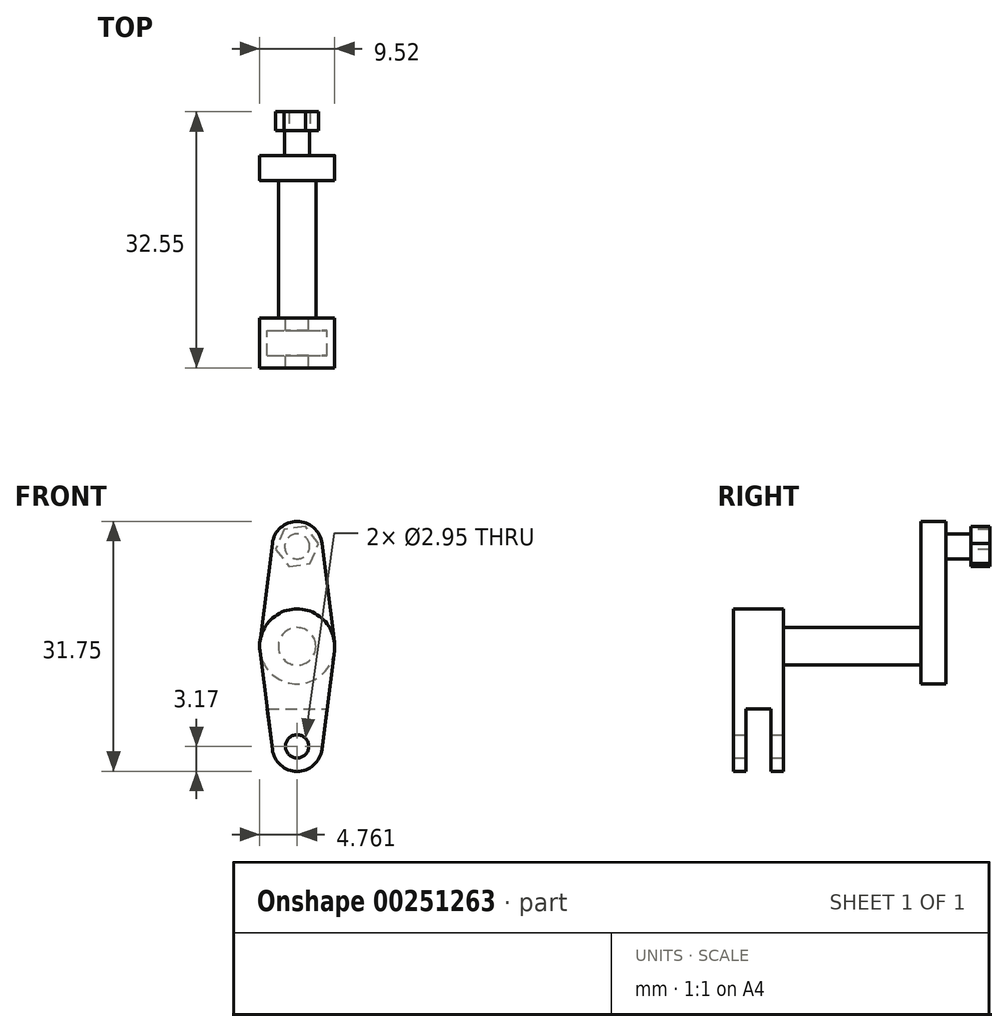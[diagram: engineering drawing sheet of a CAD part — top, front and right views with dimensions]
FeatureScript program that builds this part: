
annotation { "Feature Type Name" : "Feature", "Feature Type Description" : "" }
export const myFeature = defineFeature(function(context is Context, id is Id, definition is map)
    precondition{}
    {
        {
            var Q0;
            Q0=qCreatedBy(makeId("Front.planeOp"),FACE);
            var sketch = newSketch(context, id + "F0", { "sketchPlane" : qUnion([Q0])});
            skLineSegment(sketch, "E0.bottom", {"start": v(30.87, 50.07) * mm, "end": v(40.4, 50.07) * mm});
            skLineSegment(sketch, "E0.top", {"start": v(30.87, 15.15) * mm, "end": v(40.4, 15.15) * mm});
            skLineSegment(sketch, "E0.left", {"start": v(30.87, 50.07) * mm, "end": v(30.87, 15.15) * mm});
            skLineSegment(sketch, "E0.right", {"start": v(40.4, 50.07) * mm, "end": v(40.4, 15.15) * mm});
            skCircle(sketch, "E1", {"center": v(35.63, 45.31) * mm, "radius": 1.47 * mm});
            skCircle(sketch, "E2", {"center": v(35.63, 19.91) * mm, "radius": 1.47 * mm});
            skCircle(sketch, "E3", {"center": v(35.63, 32.61) * mm, "radius": 4.76 * mm});
            skCircle(sketch, "E4", {"center": v(35.63, 45.31) * mm, "radius": 3.18 * mm});
            skCircle(sketch, "E5", {"center": v(35.63, 19.91) * mm, "radius": 3.18 * mm});
            skLineSegment(sketch, "E6", {"start": v(32.48, 45.7) * mm, "end": v(30.9, 33.2) * mm});
            skLineSegment(sketch, "E7", {"start": v(38.78, 45.7) * mm, "end": v(40.36, 33.2) * mm});
            skLineSegment(sketch, "E8", {"start": v(30.9, 32.01) * mm, "end": v(32.48, 19.51) * mm});
            skLineSegment(sketch, "E9", {"start": v(40.36, 32.01) * mm, "end": v(38.78, 19.51) * mm});
            skSolve(sketch);
        }
        {
            var Q0;
            Q0=makeQuery(id+"F0.imprint","IMPRINT",FACE,{"disambiguationData":[TD([[makeQuery(id+"F0.imprint","IMPRINT",EDGE,{"derivedFrom":sQuery(id+"F0.wireOp",EDGE,"E1")}),1.0]])]});
            var Q1;
            Q1=makeQuery(id+"F0.imprint","IMPRINT",FACE,{"disambiguationData":[TD([[makeQuery(id+"F0.imprint","IMPRINT",EDGE,{"derivedFrom":sQuery(id+"F0.wireOp",EDGE,"E1")}),-1.0]])]});
            var Q2;
            {var subQ0=sQuery(id+"F0.wireOp",EDGE,"E6");Q2=makeQuery(id+"F0.imprint","IMPRINT",FACE,{"disambiguationData":[TD([[makeQuery(id+"F0.imprint","IMPRINT",EDGE,{"derivedFrom":subQ0}),1.0]])]});}
            var Q3;
            {var subQ0=sQuery(id+"F0.wireOp",EDGE,"E3");var subQ4=makeQuery(id+"F0.imprint","INTERSECT",VERTEX,{"derivedFrom":[subQ0,sQuery(id+"F0.wireOp",EDGE,"E7")]});Q3=makeQuery(id+"F0.imprint","IMPRINT",FACE,{"disambiguationData":[TD([[makeQuery(id+"F0.imprint","IMPRINT",EDGE,{"disambiguationData":[TD([[subQ4,1.0]])],"derivedFrom":subQ0}),1.0]])]});}
            extrude(context, id + "F1", {"entities" : qUnion([Q0, Q1, Q2, Q3]), "depth" : 3.17 * mm});
        }
        {
            var Q0;
            Q0=makeQuery(id+"F1.opExtrude","CAP_FACE",FACE,{"disambiguationData":[OSD([sQuery(id+"F0.wireOp",EDGE,"E3"),sQuery(id+"F0.wireOp",EDGE,"E4"),sQuery(id+"F0.wireOp",EDGE,"E6"),sQuery(id+"F0.wireOp",EDGE,"E7")])],"isStart":true});
            var sketch = newSketch(context, id + "F2", { "sketchPlane" : qUnion([Q0])});
            skCircle(sketch, "E10", {"center": v(-35.63, 45.31) * mm, "radius": 1.59 * mm});
            skSolve(sketch);
        }
        {
            var Q0;
            Q0 = qSketchRegion(id + "F2", true);
            extrude(context, id + "F3", {"entities" : qUnion([Q0]), "operationType" : NewBodyOperationType.ADD, "depth" : 3.17 * mm});
        }
        {
            var Q0;
            Q0=makeQuery(id+"F3.opExtrude","CAP_FACE",FACE,{"disambiguationData":[OSD([sQuery(id+"F2.wireOp",EDGE,"E10")])],"isStart":false});
            var sketch = newSketch(context, id + "F4", { "sketchPlane" : qUnion([Q0])});
            skCircle(sketch, "E11.cCircle", {"center": v(-35.63, 45.31) * mm, "radius": 2.38 * mm, "construction": true});
            skLineSegment(sketch, "E11.0", {"start": v(-32.9, 44.95) * mm, "end": v(-34.58, 42.77) * mm});
            skLineSegment(sketch, "E11.1", {"start": v(-34.58, 42.77) * mm, "end": v(-37.3, 43.13) * mm});
            skLineSegment(sketch, "E11.2", {"start": v(-37.3, 43.13) * mm, "end": v(-38.36, 45.67) * mm});
            skLineSegment(sketch, "E11.3", {"start": v(-38.36, 45.67) * mm, "end": v(-36.69, 47.85) * mm});
            skLineSegment(sketch, "E11.4", {"start": v(-36.69, 47.85) * mm, "end": v(-33.96, 47.5) * mm});
            skLineSegment(sketch, "E11.5", {"start": v(-33.96, 47.5) * mm, "end": v(-32.9, 44.95) * mm});
            skPoint(sketch, "E11.0.midPoint", {"position": v(-33.74, 43.86) * mm});
            skSolve(sketch);
        }
        {
            var Q0;
            Q0 = qSketchRegion(id + "F4", true);
            extrude(context, id + "F5", {"entities" : qUnion([Q0]), "operationType" : NewBodyOperationType.ADD, "depth" : 2.38 * mm});
        }
        {
            var Q0;
            Q0=makeQuery(id+"F1.opExtrude","CAP_FACE",FACE,{"disambiguationData":[OSD([sQuery(id+"F0.wireOp",EDGE,"E3"),sQuery(id+"F0.wireOp",EDGE,"E4"),sQuery(id+"F0.wireOp",EDGE,"E6"),sQuery(id+"F0.wireOp",EDGE,"E7")])],"isStart":false});
            var sketch = newSketch(context, id + "F6", { "sketchPlane" : qUnion([Q0])});
            skCircle(sketch, "E12", {"center": v(35.63, 32.61) * mm, "radius": 2.38 * mm});
            skSolve(sketch);
        }
        {
            var Q0;
            Q0 = qSketchRegion(id + "F6", true);
            extrude(context, id + "F7", {"entities" : qUnion([Q0]), "operationType" : NewBodyOperationType.ADD, "depth" : 17.46 * mm});
        }
        {
            var Q0;
            Q0=makeQuery(id+"F7.opExtrude","CAP_FACE",FACE,{"disambiguationData":[OSD([sQuery(id+"F6.wireOp",EDGE,"E12")])],"isStart":false});
            var sketch = newSketch(context, id + "F8", { "sketchPlane" : qUnion([Q0])});
            skCircle(sketch, "E13", {"center": v(35.63, 32.61) * mm, "radius": 4.76 * mm});
            skCircle(sketch, "E14", {"center": v(35.63, 19.91) * mm, "radius": 3.18 * mm});
            skLineSegment(sketch, "E15", {"start": v(30.9, 32.01) * mm, "end": v(32.48, 19.51) * mm});
            skLineSegment(sketch, "E16", {"start": v(40.36, 32.01) * mm, "end": v(38.78, 19.51) * mm});
            skCircle(sketch, "E17", {"center": v(35.63, 19.91) * mm, "radius": 1.47 * mm});
            skSolve(sketch);
        }
        {
            var Q0;
            Q0 = qSketchRegion(id + "F8", true);
            extrude(context, id + "F9", {"entities" : qUnion([Q0]), "operationType" : NewBodyOperationType.ADD, "depth" : 6.35 * mm});
        }
        {
            var Q0;
            Q0=makeQuery(id+"F9.opExtrude","CAP_FACE",FACE,{"disambiguationData":[OSD([sQuery(id+"F8.wireOp",EDGE,"E13"),sQuery(id+"F8.wireOp",EDGE,"E14"),sQuery(id+"F8.wireOp",EDGE,"E15"),sQuery(id+"F8.wireOp",EDGE,"E16"),sQuery(id+"F8.wireOp",EDGE,"E17")])],"isStart":false});
            cPlane(context, id + "F10", {"entities" : qUnion([Q0]), "cplaneType" : CPlaneType.OFFSET, "offset" : 3.17 * mm, "oppositeDirection" : true, "width" : 152.4 * mm, "height" : 152.4 * mm});
        }
        {
            var Q0;
            Q0=qCreatedBy(id+"F10.planeOp",FACE);
            var sketch = newSketch(context, id + "F11", { "sketchPlane" : qUnion([Q0])});
            skLineSegment(sketch, "E18.0", {"start": v(40.36, 32.01) * mm, "end": v(38.78, 19.51) * mm});
            skLineSegment(sketch, "E19.0", {"start": v(30.9, 32.01) * mm, "end": v(32.48, 19.51) * mm});
            skCircle(sketch, "E20.0", {"center": v(35.63, 19.91) * mm, "radius": 1.47 * mm});
            skArc(sketch, "E21.0", {"start": v(32.48, 19.51) * mm, "mid": v(35.63, 16.74) * mm, "end": v(38.78, 19.51) * mm});
            skLineSegment(sketch, "E22", {"start": v(31.83, 24.67) * mm, "end": v(39.43, 24.67) * mm});
            skSolve(sketch);
        }
        {
            var Q0;
            Q0 = qSketchRegion(id + "F11", true);
            extrude(context, id + "F12", {"entities" : qUnion([Q0]), "operationType" : NewBodyOperationType.REMOVE, "depth" : 3.17 * mm, "symmetric" : true});
        }
    });
